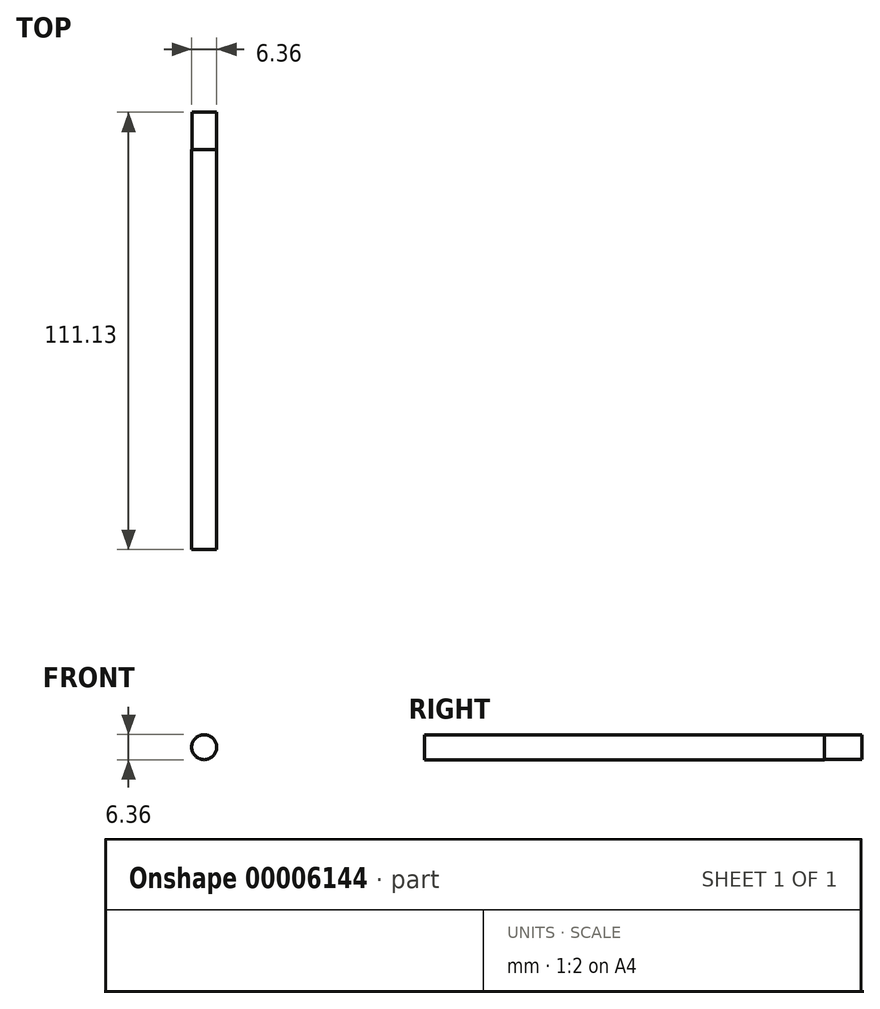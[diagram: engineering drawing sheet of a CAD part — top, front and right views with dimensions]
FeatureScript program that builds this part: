
annotation { "Feature Type Name" : "Feature", "Feature Type Description" : "" }
export const myFeature = defineFeature(function(context is Context, id is Id, definition is map)
    precondition{}
    {
        {
            var Q0;
            Q0=qCreatedBy(makeId("Front.planeOp"),FACE);
            var sketch = newSketch(context, id + "F0", { "sketchPlane" : qUnion([Q0])});
            skCircle(sketch, "E0", {"center": v(0, 0) * mm, "radius": 3.11 * mm});
            skSolve(sketch);
        }
        {
            var Q0;
            Q0 = qSketchRegion(id + "F0", true);
            extrude(context, id + "F1", {"entities" : qUnion([Q0]), "oppositeDirection" : true, "depth" : 9.52 * mm});
        }
        {
            var Q0;
            Q0=makeQuery(id+"F1.opExtrude","CAP_FACE",FACE,{"disambiguationData":[OSD([sQuery(id+"F0.wireOp",EDGE,"E0")])],"isStart":true});
            var sketch = newSketch(context, id + "F2", { "sketchPlane" : qUnion([Q0])});
            skCircle(sketch, "E1", {"center": v(0, 0) * mm, "radius": 3.18 * mm});
            skSolve(sketch);
        }
        {
            var Q0;
            Q0 = qSketchRegion(id + "F2", true);
            extrude(context, id + "F3", {"entities" : qUnion([Q0]), "operationType" : NewBodyOperationType.ADD, "depth" : 101.6 * mm});
        }
    });
